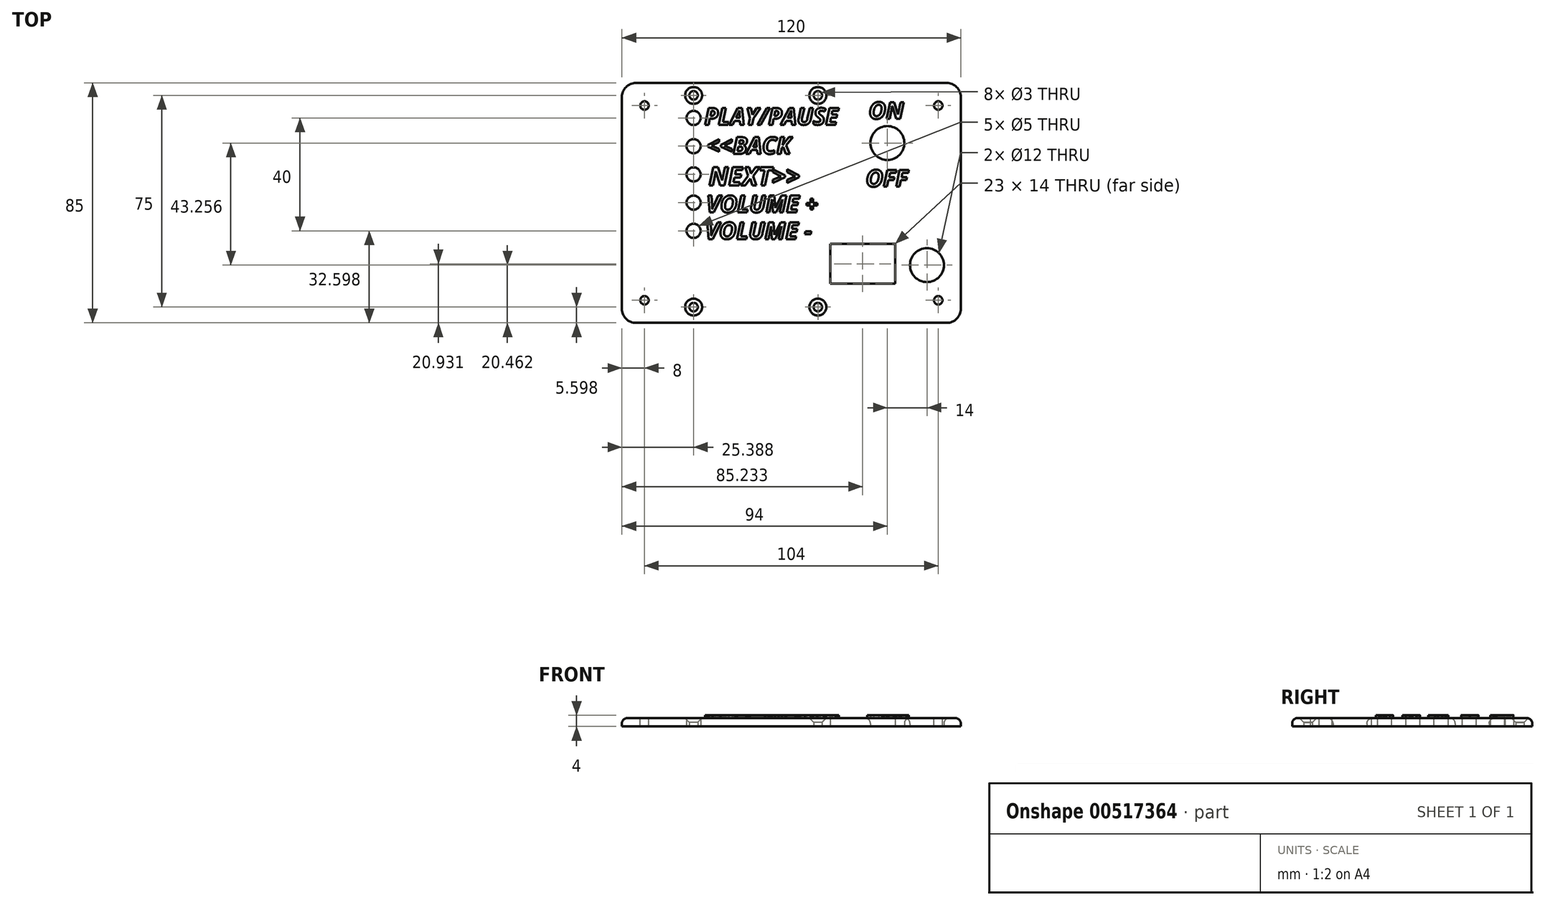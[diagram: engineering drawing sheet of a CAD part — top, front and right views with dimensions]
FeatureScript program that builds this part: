
annotation { "Feature Type Name" : "Feature", "Feature Type Description" : "" }
export const myFeature = defineFeature(function(context is Context, id is Id, definition is map)
    precondition{}
    {
        {
            var Q0;
            Q0=qCreatedBy(makeId("Top.planeOp"),FACE);
            var sketch = newSketch(context, id + "F0", { "sketchPlane" : qUnion([Q0])});
            skLineSegment(sketch, "E0.bottom", {"start": v(60, 42.5) * mm, "end": v(-60, 42.5) * mm});
            skLineSegment(sketch, "E0.top", {"start": v(60, -42.5) * mm, "end": v(-60, -42.5) * mm});
            skLineSegment(sketch, "E0.left", {"start": v(60, 42.5) * mm, "end": v(60, -42.5) * mm});
            skLineSegment(sketch, "E0.right", {"start": v(-60, 42.5) * mm, "end": v(-60, -42.5) * mm});
            skPoint(sketch, "E0.middle", {"position": v(0, 0) * mm});
            skLineSegment(sketch, "E1.bottom", {"start": v(9.39, -36.9) * mm, "end": v(9.39, 38.1) * mm, "construction": true});
            skLineSegment(sketch, "E1.top", {"start": v(-34.61, -36.9) * mm, "end": v(-34.61, 38.1) * mm, "construction": true});
            skLineSegment(sketch, "E1.left", {"start": v(9.39, -36.9) * mm, "end": v(-34.61, -36.9) * mm, "construction": true});
            skLineSegment(sketch, "E1.right", {"start": v(9.39, 38.1) * mm, "end": v(-34.61, 38.1) * mm, "construction": true});
            skPoint(sketch, "E1.middle", {"position": v(-12.61, 0.6) * mm});
            skCircle(sketch, "E2", {"center": v(9.39, 38.1) * mm, "radius": 1.5 * mm});
            skCircle(sketch, "E3", {"center": v(9.39, -36.9) * mm, "radius": 1.5 * mm});
            skCircle(sketch, "E4", {"center": v(-34.61, -36.9) * mm, "radius": 1.5 * mm});
            skCircle(sketch, "E5", {"center": v(-34.61, 38.1) * mm, "radius": 1.5 * mm});
            skCircle(sketch, "E6", {"center": v(-34.61, 30.1) * mm, "radius": 2.5 * mm});
            skCircle(sketch, "E7", {"center": v(-34.61, 20.1) * mm, "radius": 2.5 * mm});
            skCircle(sketch, "E8", {"center": v(-34.61, 10.1) * mm, "radius": 2.5 * mm});
            skCircle(sketch, "E9", {"center": v(-34.61, 0.1) * mm, "radius": 2.5 * mm});
            skCircle(sketch, "E10", {"center": v(-34.61, -9.9) * mm, "radius": 2.5 * mm});
            skCircle(sketch, "E11", {"center": v(34, 21.22) * mm, "radius": 6 * mm});
            skLineSegment(sketch, "E12", {"start": v(34, 21.22) * mm, "end": v(34, -50.36) * mm, "construction": true});
            skPoint(sketch, "E13.middle", {"position": v(34, -22.08) * mm});
            skLineSegment(sketch, "E14.bottom", {"start": v(36.73, -14.57) * mm, "end": v(13.73, -14.57) * mm});
            skLineSegment(sketch, "E14.top", {"start": v(36.73, -28.57) * mm, "end": v(13.73, -28.57) * mm});
            skLineSegment(sketch, "E14.left", {"start": v(36.73, -14.57) * mm, "end": v(36.73, -28.57) * mm});
            skLineSegment(sketch, "E14.right", {"start": v(13.73, -14.57) * mm, "end": v(13.73, -28.57) * mm});
            skPoint(sketch, "E14.middle", {"position": v(25.23, -21.57) * mm});
            skPoint(sketch, "E14.cornerSnap0", {"position": v(34, -14.57) * mm});
            skCircle(sketch, "E15", {"center": v(48, -22.04) * mm, "radius": 6 * mm});
            skSolve(sketch);
        }
        {
            var Q0;
            Q0 = qSketchRegion(id + "F0", true);
            extrude(context, id + "F1", {"entities" : qUnion([Q0]), "depth" : 3 * mm, "offsetDistance" : 25 * mm});
        }
        {
            var Q0;
            Q0=makeQuery(id+"F1.opExtrude","CAP_FACE",FACE,{"disambiguationData":[OSD([sQuery(id+"F0.wireOp",EDGE,"E0.bottom"),sQuery(id+"F0.wireOp",EDGE,"E0.top"),sQuery(id+"F0.wireOp",EDGE,"E0.left"),sQuery(id+"F0.wireOp",EDGE,"E0.right"),sQuery(id+"F0.wireOp",EDGE,"E2"),sQuery(id+"F0.wireOp",EDGE,"E3"),sQuery(id+"F0.wireOp",EDGE,"E4"),sQuery(id+"F0.wireOp",EDGE,"E5"),sQuery(id+"F0.wireOp",EDGE,"E6"),sQuery(id+"F0.wireOp",EDGE,"E7"),sQuery(id+"F0.wireOp",EDGE,"E8"),sQuery(id+"F0.wireOp",EDGE,"E9"),sQuery(id+"F0.wireOp",EDGE,"E10"),sQuery(id+"F0.wireOp",EDGE,"E11"),sQuery(id+"F0.wireOp",EDGE,"E13.bottom"),sQuery(id+"F0.wireOp",EDGE,"E13.top"),sQuery(id+"F0.wireOp",EDGE,"E13.left"),sQuery(id+"F0.wireOp",EDGE,"E13.right")])],"isStart":false});
            var sketch = newSketch(context, id + "F2", { "sketchPlane" : qUnion([Q0])});
            skText(sketch, "E16", { "text": "PLAY/PAUSE", "fontName": "OpenSans-BoldItalic.ttf"});
            skText(sketch, "E17", { "text": "<<BACK", "fontName": "OpenSans-BoldItalic.ttf"});
            skText(sketch, "E18", { "text": "NEXT>>", "fontName": "OpenSans-BoldItalic.ttf"});
            skText(sketch, "E19", { "text": "VOLUME +", "fontName": "OpenSans-BoldItalic.ttf"});
            skText(sketch, "E20", { "text": "VOLUME -", "fontName": "OpenSans-BoldItalic.ttf"});
            const initialGuessF2  = {"E16": [-0.03076, 0.02767, 1, 0, 0.006], "E17": [-0.02994, 0.01734, 1, 0, 0.006], "E18": [-0.02923, 0.0062, 1, 0, 0.00658], "E19": [-0.03018, -0.00337, 1, 0, 0.006], "E20": [-0.03051, -0.01284, 1, 0, 0.006]};
            skSetInitialGuess(sketch, initialGuessF2);
            skSolve(sketch);
        }
        {
            var Q0;
            Q0 = qSketchRegion(id + "F2", true);
            extrude(context, id + "F3", {"entities" : qUnion([Q0]), "operationType" : NewBodyOperationType.ADD, "depth" : 1 * mm, "offsetDistance" : 25 * mm});
        }
        {
            var Q0;
            {var subQ0=sQuery(id+"F0.wireOp",EDGE,"E6");var subQ1=sQuery(id+"F0.wireOp",EDGE,"E5");var subQ2=sQuery(id+"F0.wireOp",EDGE,"E4");var subQ3=sQuery(id+"F0.wireOp",EDGE,"E3");var subQ4=sQuery(id+"F0.wireOp",EDGE,"E2");var subQ5=sQuery(id+"F0.wireOp",EDGE,"E7");var subQ6=sQuery(id+"F0.wireOp",EDGE,"E0.bottom");var subQ7=sQuery(id+"F0.wireOp",EDGE,"E0.right");var subQ8=sQuery(id+"F0.wireOp",EDGE,"E0.top");var subQ9=sQuery(id+"F0.wireOp",EDGE,"E0.left");var subQ10=sQuery(id+"F0.wireOp",EDGE,"E8");var subQ11=sQuery(id+"F0.wireOp",EDGE,"E9");var subQ12=sQuery(id+"F0.wireOp",EDGE,"E10");var subQ13=sQuery(id+"F0.wireOp",EDGE,"E11");var subQ14=sQuery(id+"F0.wireOp",EDGE,"E13.bottom");var subQ15=sQuery(id+"F0.wireOp",EDGE,"E13.top");var subQ16=sQuery(id+"F0.wireOp",EDGE,"E13.left");var subQ17=sQuery(id+"F0.wireOp",EDGE,"E13.right");Q0=makeQuery(id+"F3.boolean.opBoolean","SPLIT",FACE,{"disambiguationData":[TD([makeQuery(id+"F1.opExtrude","SWEPT_FACE",FACE,{"disambiguationData":[OSD([subQ6])]})])],"derivedFrom":makeQuery(id+"F1.opExtrude","CAP_FACE",FACE,{"disambiguationData":[OSD([subQ6,subQ8,subQ9,subQ7,subQ4,subQ3,subQ2,subQ1,subQ0,subQ5,subQ10,subQ11,subQ12,subQ13,subQ14,subQ15,subQ16,subQ17])],"isStart":false})});}
            var sketch = newSketch(context, id + "F4", { "sketchPlane" : qUnion([Q0])});
            skText(sketch, "E21", { "text": "ON", "fontName": "OpenSans-BoldItalic.ttf"});
            skText(sketch, "E22", { "text": "OFF", "fontName": "OpenSans-BoldItalic.ttf"});
            const initialGuessF4  = {"E21": [0.02737, 0.02976, 1, 0, 0.006], "E22": [0.02635, 0.00575, 1, 0, 0.006]};
            skSetInitialGuess(sketch, initialGuessF4);
            skSolve(sketch);
        }
        {
            var Q0;
            Q0 = qSketchRegion(id + "F4", true);
            extrude(context, id + "F5", {"entities" : qUnion([Q0]), "operationType" : NewBodyOperationType.ADD, "depth" : 1 * mm, "offsetDistance" : 25 * mm});
        }
        {
            var Q0;
            {var subQ68=sQuery(id+"F0.wireOp",EDGE,"E7");var subQ71=sQuery(id+"F0.wireOp",EDGE,"E6");var subQ74=sQuery(id+"F0.wireOp",EDGE,"E5");var subQ77=sQuery(id+"F0.wireOp",EDGE,"E4");var subQ80=sQuery(id+"F0.wireOp",EDGE,"E3");var subQ83=sQuery(id+"F0.wireOp",EDGE,"E2");var subQ86=sQuery(id+"F0.wireOp",EDGE,"E0.right");var subQ89=sQuery(id+"F0.wireOp",EDGE,"E0.left");var subQ92=sQuery(id+"F0.wireOp",EDGE,"E0.top");var subQ95=sQuery(id+"F0.wireOp",EDGE,"E0.bottom");var subQ96=makeQuery(id+"F1.opExtrude","SWEPT_FACE",FACE,{"disambiguationData":[OSD([subQ95])]});var subQ220=sQuery(id+"F0.wireOp",EDGE,"E13.right");var subQ223=sQuery(id+"F0.wireOp",EDGE,"E13.left");var subQ226=sQuery(id+"F0.wireOp",EDGE,"E13.top");var subQ231=sQuery(id+"F0.wireOp",EDGE,"E13.bottom");var subQ240=sQuery(id+"F0.wireOp",EDGE,"E11");var subQ250=sQuery(id+"F0.wireOp",EDGE,"E10");var subQ261=sQuery(id+"F0.wireOp",EDGE,"E9");var subQ273=sQuery(id+"F0.wireOp",EDGE,"E8");Q0=makeQuery(id+"F5.boolean.opBoolean","SPLIT",FACE,{"disambiguationData":[TD([subQ96])],"derivedFrom":makeQuery(id+"F3.boolean.opBoolean","SPLIT",FACE,{"disambiguationData":[TD([subQ96])],"derivedFrom":makeQuery(id+"F1.opExtrude","CAP_FACE",FACE,{"disambiguationData":[OSD([subQ95,subQ92,subQ89,subQ86,subQ83,subQ80,subQ77,subQ74,subQ71,subQ68,subQ273,subQ261,subQ250,subQ240,subQ231,subQ226,subQ223,subQ220])],"isStart":false})})});}
            var sketch = newSketch(context, id + "F6", { "sketchPlane" : qUnion([Q0])});
            skCircle(sketch, "E23", {"center": v(-52, 34.5) * mm, "radius": 1.5 * mm});
            skCircle(sketch, "E24.MirrorC", {"center": v(52, 34.5) * mm, "radius": 1.5 * mm});
            skCircle(sketch, "E25.MirrorC", {"center": v(-52, -34.5) * mm, "radius": 1.5 * mm});
            skCircle(sketch, "E26.MirrorC", {"center": v(52, -34.5) * mm, "radius": 1.5 * mm});
            skSolve(sketch);
        }
        {
            var Q0;
            Q0 = qSketchRegion(id + "F6", true);
            extrude(context, id + "F7", {"entities" : qUnion([Q0]), "operationType" : NewBodyOperationType.REMOVE, "oppositeDirection" : true, "depth" : 5 * mm, "offsetDistance" : 25 * mm});
        }
        {
            var Q0;
            Q0=makeQuery(id+"F1.opExtrude","SWEPT_EDGE",EDGE,{"disambiguationData":[OSD([sQuery(id+"F0.wireOp",EDGE,"E0.bottom"),sQuery(id+"F0.wireOp",EDGE,"E0.right")])]});
            var Q1;
            Q1=makeQuery(id+"F1.opExtrude","SWEPT_EDGE",EDGE,{"disambiguationData":[OSD([sQuery(id+"F0.wireOp",EDGE,"E0.bottom"),sQuery(id+"F0.wireOp",EDGE,"E0.left")])]});
            var Q2;
            Q2=makeQuery(id+"F1.opExtrude","SWEPT_EDGE",EDGE,{"disambiguationData":[OSD([sQuery(id+"F0.wireOp",EDGE,"E0.top"),sQuery(id+"F0.wireOp",EDGE,"E0.left")])]});
            var Q3;
            Q3=makeQuery(id+"F1.opExtrude","SWEPT_EDGE",EDGE,{"disambiguationData":[OSD([sQuery(id+"F0.wireOp",EDGE,"E0.top"),sQuery(id+"F0.wireOp",EDGE,"E0.right")])]});
            fillet(context, id + "F8", {"entities" : qUnion([Q0, Q1, Q2, Q3]), "radius" : 5 * mm, "tangentPropagation" : true, "allowEdgeOverflow" : false});
        }
        {
            var Q0;
            Q0=makeQuery(id+"F1.opExtrude","CAP_EDGE",EDGE,{"disambiguationData":[OSD([sQuery(id+"F0.wireOp",EDGE,"E0.top")])],"isStart":false});
            fillet(context, id + "F9", {"entities" : qUnion([Q0]), "radius" : 2 * mm, "tangentPropagation" : true, "allowEdgeOverflow" : false});
        }
        {
            var Q0;
            Q0=makeQuery(id+"F1.opExtrude","CAP_EDGE",EDGE,{"disambiguationData":[OSD([sQuery(id+"F0.wireOp",EDGE,"E11")])],"isStart":false});
            var Q1;
            Q1=makeQuery(id+"F1.opExtrude","CAP_EDGE",EDGE,{"disambiguationData":[OSD([sQuery(id+"F0.wireOp",EDGE,"E15")])],"isStart":false});
            fillet(context, id + "F10", {"entities" : qUnion([Q0, Q1]), "radius" : 2 * mm, "tangentPropagation" : true, "allowEdgeOverflow" : false});
        }
        {
            var Q0;
            Q0=makeQuery(id+"F1.opExtrude","CAP_EDGE",EDGE,{"disambiguationData":[OSD([sQuery(id+"F0.wireOp",EDGE,"E5")])],"isStart":false});
            var Q1;
            Q1=makeQuery(id+"F1.opExtrude","CAP_EDGE",EDGE,{"disambiguationData":[OSD([sQuery(id+"F0.wireOp",EDGE,"E2")])],"isStart":false});
            var Q2;
            Q2=makeQuery(id+"F1.opExtrude","CAP_EDGE",EDGE,{"disambiguationData":[OSD([sQuery(id+"F0.wireOp",EDGE,"E3")])],"isStart":false});
            var Q3;
            Q3=makeQuery(id+"F1.opExtrude","CAP_EDGE",EDGE,{"disambiguationData":[OSD([sQuery(id+"F0.wireOp",EDGE,"E4")])],"isStart":false});
            chamfer(context, id + "F11", {"entities" : qUnion([Q0, Q1, Q2, Q3]), "width" : 1.5 * mm, "tangentPropagation" : true});
        }
    });
